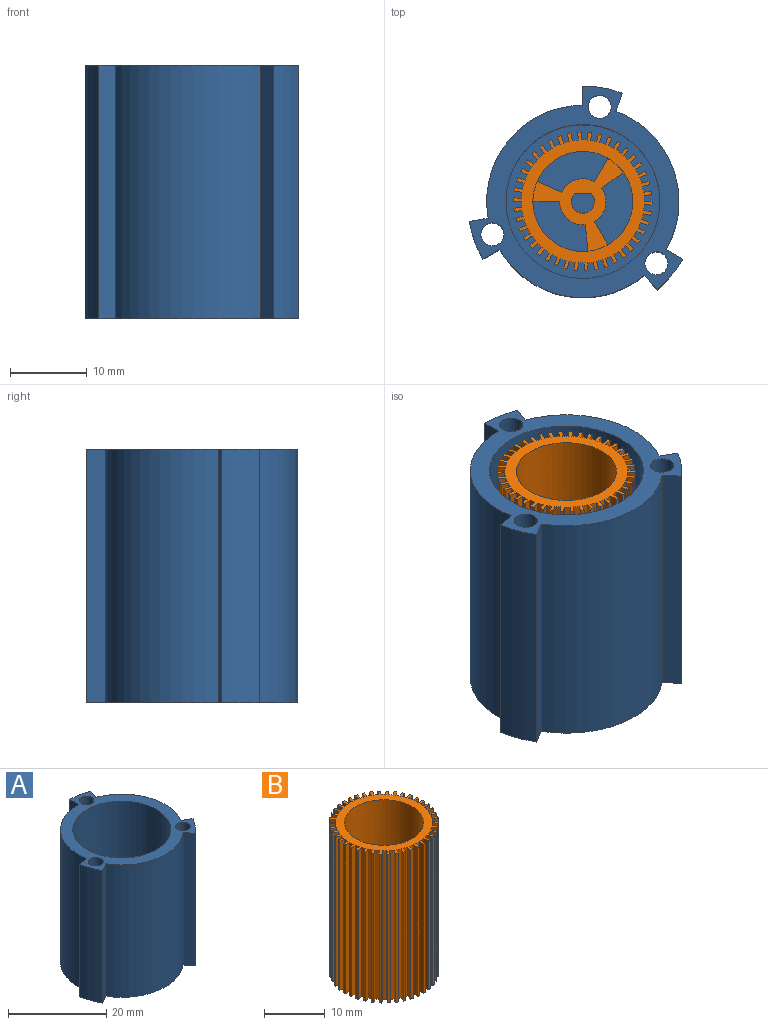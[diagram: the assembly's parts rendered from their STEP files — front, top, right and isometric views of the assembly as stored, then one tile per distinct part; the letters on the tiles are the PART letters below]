
ASSEMBLY  parts=2 mates=1
PART A: 22 faces, bbox 27.8x27.5x33 mm
  f0: plane 33x2.35mm, normal (0.94,-0.34,0), area 82.5mm2, adj f1,f14,f16,f18
  f1: cylinder r=15mm len=33mm, axis (0,0,-1), area 172.8mm2, adj f0,f2,f16,f18
  f2: plane 33x2.5mm, normal (-1,0,0), area 82.5mm2, adj f1,f3,f16,f18
  f3: cylinder r=12.5mm len=33mm, axis (0,0,-1), area 719.9mm2, adj f2,f4,f16,f18
  f4: plane 33x2.46mm, normal (-0.17,0.98,0), area 82.5mm2, adj f3,f5,f16,f18
  f5: cylinder r=15mm len=33mm, axis (0,0,-1), area 172.8mm2, adj f4,f6,f16,f18
  f6: plane 33x2.17mm, normal (0.5,-0.87,0), area 82.5mm2, adj f5,f7,f16,f18
  f7: cylinder r=12.5mm len=33mm, axis (0,0,-1), area 719.9mm2, adj f6,f8,f16,f18
  f8: plane 33x1.92mm, normal (-0.77,-0.64,0), area 82.5mm2, adj f7,f9,f16,f18
  f9: cylinder r=15mm len=33mm, axis (0,0,-1), area 172.8mm2, adj f8,f10,f16,f18
  f10: plane 33x2.17mm, normal (0.5,0.87,0), area 82.5mm2, adj f9,f14,f16,f18
  f11: cylinder r=1.5mm len=33mm, axis (0,0,-1), area 311mm2, adj f16,f18
  f12: cylinder r=1.5mm len=33mm, axis (0,0,-1), area 311mm2, adj f16,f18
  f13: cylinder r=1.5mm len=33mm, axis (0,0,-1), area 311mm2, adj f16,f18
  f14: cylinder r=12.5mm len=33mm, axis (0,0,-1), area 719.9mm2, adj f0,f10,f16,f18
  f15: plane 20x20mm, normal (0,0,1), area 307.9mm2, adj f17,f20,f21
  f16: plane 27.76x27.5mm, normal (0,0,-1), area 505.7mm2, adj f0,f1,f2,f3,f4,f5,f6,f7
  f17: cylinder r=10mm len=30mm, axis (0,0,-1), area 1885mm2, adj f15,f18
  f18: plane 27.76x27.5mm, normal (0,0,1), area 191.5mm2, adj f0,f1,f2,f3,f4,f5,f6,f7
  f19: plane 3x2.5mm, normal (0,0,1), area 6.3mm2, adj f20,f21
  f20: cylinder r=1.5mm len=17mm, axis (0,0,-1), area 117.3mm2, adj f15,f19,f21
  f21: plane 17x2.24mm, normal (0,1,0), area 38mm2, adj f15,f19,f20
PART B: 183 faces, bbox 18x18x30 mm
  f0: plane 18x18mm, normal (0,0,-1), area 129.9mm2, adj f1,f2,f3,f4,f5,f6,f7,f8
  f1: cylinder r=3mm len=10mm, axis (0,0,-1), area 50.3mm2, adj f0,f176,f179,f182
  f2: cylinder r=3mm len=10mm, axis (0,0,-1), area 50.3mm2, adj f0,f176,f177,f180
  f3: cylinder r=3mm len=10mm, axis (0,0,-1), area 50.3mm2, adj f0,f176,f178,f181
  f4: cylinder r=6.5mm len=30mm, axis (0,0,-1), area 1143.5mm2, adj f0,f173,f176,f177,f178,f179,f180,f181
  f5: cylinder r=8mm len=30mm, axis (0,0,-1), area 23.3mm2, adj f0,f6,f172,f173
  f6: plane 30x1mm, normal (-0.05,-1,0), area 30mm2, adj f0,f5,f7,f173
  f7: cylinder r=9mm len=30mm, axis (0,0,-1), area 14.1mm2, adj f0,f6,f8,f173
  f8: plane 30x1mm, normal (0,1,0), area 30mm2, adj f0,f7,f9,f173
  f9: cylinder r=8mm len=30mm, axis (0,0,-1), area 23.3mm2, adj f0,f8,f10,f173
  f10: plane 30x1mm, normal (0.1,-1,0), area 30mm2, adj f0,f9,f11,f173
  f11: cylinder r=9mm len=30mm, axis (0,0,-1), area 14.1mm2, adj f0,f10,f12,f173
  f12: plane 30x0.99mm, normal (-0.15,0.99,0), area 30mm2, adj f0,f11,f13,f173
  f13: cylinder r=8mm len=30mm, axis (0,0,-1), area 23.3mm2, adj f0,f12,f14,f173
  f14: plane 30x0.97mm, normal (0.24,-0.97,0), area 30mm2, adj f0,f13,f15,f173
  f15: cylinder r=9mm len=30mm, axis (0,0,-1), area 14.1mm2, adj f0,f14,f16,f173
  f16: plane 30x0.96mm, normal (-0.29,0.96,0), area 30mm2, adj f0,f15,f17,f173
  f17: cylinder r=8mm len=30mm, axis (0,0,-1), area 23.3mm2, adj f0,f16,f18,f173
  f18: plane 30x0.92mm, normal (0.39,-0.92,0), area 30mm2, adj f0,f17,f19,f173
  f19: cylinder r=9mm len=30mm, axis (0,0,-1), area 14.1mm2, adj f0,f18,f20,f173
  f20: plane 30x0.9mm, normal (-0.43,0.9,0), area 30mm2, adj f0,f19,f21,f173
  f21: cylinder r=8mm len=30mm, axis (0,0,-1), area 23.3mm2, adj f0,f20,f22,f173
  f22: plane 30x0.85mm, normal (0.52,-0.85,0), area 30mm2, adj f0,f21,f23,f173
  f23: cylinder r=9mm len=30mm, axis (0,0,-1), area 14.1mm2, adj f0,f22,f24,f173
  f24: plane 30x0.83mm, normal (-0.56,0.83,0), area 30mm2, adj f0,f23,f25,f173
  f25: cylinder r=8mm len=30mm, axis (0,0,-1), area 23.3mm2, adj f0,f24,f26,f173
  f26: plane 30x0.77mm, normal (0.64,-0.77,0), area 30mm2, adj f0,f25,f27,f173
  f27: cylinder r=9mm len=30mm, axis (0,0,-1), area 14.1mm2, adj f0,f26,f28,f173
  f28: plane 30x0.73mm, normal (-0.68,0.73,0), area 30mm2, adj f0,f27,f29,f173
  f29: cylinder r=8mm len=30mm, axis (0,0,-1), area 23.3mm2, adj f0,f28,f30,f173
  f30: plane 30x0.75mm, normal (0.75,-0.66,0), area 30mm2, adj f0,f29,f31,f173
  f31: cylinder r=9mm len=30mm, axis (0,0,-1), area 14.1mm2, adj f0,f30,f32,f173
  f32: plane 30x0.78mm, normal (-0.78,0.62,0), area 30mm2, adj f0,f31,f33,f173
  f33: cylinder r=8mm len=30mm, axis (0,0,-1), area 23.3mm2, adj f0,f32,f34,f173
  f34: plane 30x0.84mm, normal (0.84,-0.54,0), area 30mm2, adj f0,f33,f35,f173
  f35: cylinder r=9mm len=30mm, axis (0,0,-1), area 14.1mm2, adj f0,f34,f36,f173
  f36: plane 30x0.87mm, normal (-0.87,0.5,0), area 30mm2, adj f0,f35,f37,f173
  f37: cylinder r=8mm len=30mm, axis (0,0,-1), area 23.3mm2, adj f0,f36,f38,f173
  f38: plane 30x0.91mm, normal (0.91,-0.41,0), area 30mm2, adj f0,f37,f39,f173
  f39: cylinder r=9mm len=30mm, axis (0,0,-1), area 14.1mm2, adj f0,f38,f40,f173
  f40: plane 30x0.93mm, normal (-0.93,0.37,0), area 30mm2, adj f0,f39,f41,f173
  f41: cylinder r=8mm len=30mm, axis (0,0,-1), area 23.3mm2, adj f0,f40,f42,f173
  f42: plane 30x0.96mm, normal (0.96,-0.27,0), area 30mm2, adj f0,f41,f43,f173
  f43: cylinder r=9mm len=30mm, axis (0,0,-1), area 14.1mm2, adj f0,f42,f44,f173
  f44: plane 30x0.98mm, normal (-0.97,0.22,0), area 30mm2, adj f0,f43,f45,f173
  f45: cylinder r=8mm len=30mm, axis (0,0,-1), area 23.3mm2, adj f0,f44,f46,f173
  f46: plane 30x0.99mm, normal (0.99,-0.13,0), area 30mm2, adj f0,f45,f47,f173
  f47: cylinder r=9mm len=30mm, axis (0,0,-1), area 14.1mm2, adj f0,f46,f48,f173
  f48: plane 30x1mm, normal (-1,0.07,0), area 30mm2, adj f0,f47,f49,f173
  f49: cylinder r=8mm len=30mm, axis (0,0,-1), area 23.3mm2, adj f0,f48,f50,f173
  f50: plane 30x1mm, normal (1,0.02,0), area 30mm2, adj f0,f49,f51,f173
  f51: cylinder r=9mm len=30mm, axis (0,0,-1), area 14.1mm2, adj f0,f50,f52,f173
  f52: plane 30x1mm, normal (-1,-0.07,0), area 30mm2, adj f0,f51,f53,f173
  f53: cylinder r=8mm len=30mm, axis (0,0,-1), area 23.3mm2, adj f0,f52,f54,f173
  f54: plane 30x0.99mm, normal (0.99,0.17,0), area 30mm2, adj f0,f53,f55,f173
  f55: cylinder r=9mm len=30mm, axis (0,0,-1), area 14.1mm2, adj f0,f54,f56,f173
  f56: plane 30x0.98mm, normal (-0.97,-0.22,0), area 30mm2, adj f0,f55,f57,f173
  f57: cylinder r=8mm len=30mm, axis (0,0,-1), area 23.3mm2, adj f0,f56,f58,f173
  f58: plane 30x0.95mm, normal (0.95,0.32,0), area 30mm2, adj f0,f57,f59,f173
  f59: cylinder r=9mm len=30mm, axis (0,0,-1), area 14.1mm2, adj f0,f58,f60,f173
  f60: plane 30x0.93mm, normal (-0.93,-0.37,0), area 30mm2, adj f0,f59,f61,f173
  f61: cylinder r=8mm len=30mm, axis (0,0,-1), area 23.3mm2, adj f0,f60,f62,f173
  f62: plane 30x0.89mm, normal (0.89,0.45,0), area 30mm2, adj f0,f61,f63,f173
  f63: cylinder r=9mm len=30mm, axis (0,0,-1), area 14.1mm2, adj f0,f62,f64,f173
  f64: plane 30x0.87mm, normal (-0.87,-0.5,0), area 30mm2, adj f0,f63,f65,f173
  f65: cylinder r=8mm len=30mm, axis (0,0,-1), area 23.3mm2, adj f0,f64,f66,f173
  f66: plane 30x0.81mm, normal (0.81,0.58,0), area 30mm2, adj f0,f65,f67,f173
  f67: cylinder r=9mm len=30mm, axis (0,0,-1), area 14.1mm2, adj f0,f66,f68,f173
  f68: plane 30x0.78mm, normal (-0.78,-0.62,0), area 30mm2, adj f0,f67,f69,f173
  f69: cylinder r=8mm len=30mm, axis (0,0,-1), area 23.3mm2, adj f0,f68,f70,f173
  f70: plane 30x0.72mm, normal (0.72,0.7,0), area 30mm2, adj f0,f69,f71,f173
  f71: cylinder r=9mm len=30mm, axis (0,0,-1), area 14.1mm2, adj f0,f70,f72,f173
  f72: plane 30x0.73mm, normal (-0.68,-0.73,0), area 30mm2, adj f0,f71,f73,f173
  f73: cylinder r=8mm len=30mm, axis (0,0,-1), area 23.3mm2, adj f0,f72,f74,f173
  f74: plane 30x0.8mm, normal (0.61,0.8,0), area 30mm2, adj f0,f73,f75,f173
  f75: cylinder r=9mm len=30mm, axis (0,0,-1), area 14.1mm2, adj f0,f74,f76,f173
  f76: plane 30x0.83mm, normal (-0.56,-0.83,0), area 30mm2, adj f0,f75,f77,f173
  f77: cylinder r=8mm len=30mm, axis (0,0,-1), area 23.3mm2, adj f0,f76,f78,f173
  f78: plane 30x0.88mm, normal (0.48,0.88,0), area 30mm2, adj f0,f77,f79,f173
  f79: cylinder r=9mm len=30mm, axis (0,0,-1), area 14.1mm2, adj f0,f78,f80,f173
  f80: plane 30x0.9mm, normal (-0.43,-0.9,0), area 30mm2, adj f0,f79,f81,f173
  f81: cylinder r=8mm len=30mm, axis (0,0,-1), area 23.3mm2, adj f0,f80,f82,f173
  f82: plane 30x0.94mm, normal (0.34,0.94,0), area 30mm2, adj f0,f81,f83,f173
  f83: cylinder r=9mm len=30mm, axis (0,0,-1), area 14.1mm2, adj f0,f82,f84,f173
  f84: plane 30x0.96mm, normal (-0.29,-0.96,0), area 30mm2, adj f0,f83,f85,f173
  f85: cylinder r=8mm len=30mm, axis (0,0,-1), area 23.3mm2, adj f0,f84,f86,f173
  f86: plane 30x0.98mm, normal (0.2,0.98,0), area 30mm2, adj f0,f85,f87,f173
  f87: cylinder r=9mm len=30mm, axis (0,0,-1), area 14.1mm2, adj f0,f86,f88,f173
  f88: plane 30x0.99mm, normal (-0.15,-0.99,0), area 30mm2, adj f0,f87,f89,f173
  f89: cylinder r=8mm len=30mm, axis (0,0,-1), area 23.3mm2, adj f0,f88,f90,f173
  f90: plane 30x1mm, normal (0.05,1,0), area 30mm2, adj f0,f89,f91,f173
  f91: cylinder r=9mm len=30mm, axis (0,0,-1), area 14.1mm2, adj f0,f90,f92,f173
  f92: plane 30x1mm, normal (0,-1,0), area 30mm2, adj f0,f91,f93,f173
  f93: cylinder r=8mm len=30mm, axis (0,0,-1), area 23.3mm2, adj f0,f92,f94,f173
  f94: plane 30x1mm, normal (-0.1,1,0), area 30mm2, adj f0,f93,f95,f173
  f95: cylinder r=9mm len=30mm, axis (0,0,-1), area 14.1mm2, adj f0,f94,f96,f173
  f96: plane 30x0.99mm, normal (0.15,-0.99,0), area 30mm2, adj f0,f95,f97,f173
  f97: cylinder r=8mm len=30mm, axis (0,0,-1), area 23.3mm2, adj f0,f96,f98,f173
  f98: plane 30x0.97mm, normal (-0.24,0.97,0), area 30mm2, adj f0,f97,f99,f173
  f99: cylinder r=9mm len=30mm, axis (0,0,-1), area 14.1mm2, adj f0,f98,f100,f173
  f100: plane 30x0.96mm, normal (0.29,-0.96,0), area 30mm2, adj f0,f99,f101,f173
  f101: cylinder r=8mm len=30mm, axis (0,0,-1), area 23.3mm2, adj f0,f100,f102,f173
  f102: plane 30x0.92mm, normal (-0.39,0.92,0), area 30mm2, adj f0,f101,f103,f173
  f103: cylinder r=9mm len=30mm, axis (0,0,-1), area 14.1mm2, adj f0,f102,f104,f173
  f104: plane 30x0.9mm, normal (0.43,-0.9,0), area 30mm2, adj f0,f103,f105,f173
  f105: cylinder r=8mm len=30mm, axis (0,0,-1), area 23.3mm2, adj f0,f104,f106,f173
  f106: plane 30x0.85mm, normal (-0.52,0.85,0), area 30mm2, adj f0,f105,f107,f173
  f107: cylinder r=9mm len=30mm, axis (0,0,-1), area 14.1mm2, adj f0,f106,f108,f173
  f108: plane 30x0.83mm, normal (0.56,-0.83,0), area 30mm2, adj f0,f107,f109,f173
  f109: cylinder r=8mm len=30mm, axis (0,0,-1), area 23.3mm2, adj f0,f108,f110,f173
  f110: plane 30x0.77mm, normal (-0.64,0.77,0), area 30mm2, adj f0,f109,f111,f173
  f111: cylinder r=9mm len=30mm, axis (0,0,-1), area 14.1mm2, adj f0,f110,f112,f173
  f112: plane 30x0.73mm, normal (0.68,-0.73,0), area 30mm2, adj f0,f111,f113,f173
  f113: cylinder r=8mm len=30mm, axis (0,0,-1), area 23.3mm2, adj f0,f112,f114,f173
  f114: plane 30x0.75mm, normal (-0.75,0.66,0), area 30mm2, adj f0,f113,f115,f173
  f115: cylinder r=9mm len=30mm, axis (0,0,-1), area 14.1mm2, adj f0,f114,f116,f173
  f116: plane 30x0.78mm, normal (0.78,-0.62,0), area 30mm2, adj f0,f115,f117,f173
  f117: cylinder r=8mm len=30mm, axis (0,0,-1), area 23.3mm2, adj f0,f116,f118,f173
  f118: plane 30x0.84mm, normal (-0.84,0.54,0), area 30mm2, adj f0,f117,f119,f173
  f119: cylinder r=9mm len=30mm, axis (0,0,-1), area 14.1mm2, adj f0,f118,f120,f173
  f120: plane 30x0.87mm, normal (0.87,-0.5,0), area 30mm2, adj f0,f119,f121,f173
  f121: cylinder r=8mm len=30mm, axis (0,0,-1), area 23.3mm2, adj f0,f120,f122,f173
  f122: plane 30x0.91mm, normal (-0.91,0.41,0), area 30mm2, adj f0,f121,f123,f173
  f123: cylinder r=9mm len=30mm, axis (0,0,-1), area 14.1mm2, adj f0,f122,f124,f173
  f124: plane 30x0.93mm, normal (0.93,-0.37,0), area 30mm2, adj f0,f123,f125,f173
  f125: cylinder r=8mm len=30mm, axis (0,0,-1), area 23.3mm2, adj f0,f124,f126,f173
  f126: plane 30x0.96mm, normal (-0.96,0.27,0), area 30mm2, adj f0,f125,f127,f173
  f127: cylinder r=9mm len=30mm, axis (0,0,-1), area 14.1mm2, adj f0,f126,f128,f173
  f128: plane 30x0.98mm, normal (0.97,-0.22,0), area 30mm2, adj f0,f127,f129,f173
  f129: cylinder r=8mm len=30mm, axis (0,0,-1), area 23.3mm2, adj f0,f128,f130,f173
  f130: plane 30x0.99mm, normal (-0.99,0.13,0), area 30mm2, adj f0,f129,f131,f173
  f131: cylinder r=9mm len=30mm, axis (0,0,-1), area 14.1mm2, adj f0,f130,f132,f173
  f132: plane 30x1mm, normal (1,-0.07,0), area 30mm2, adj f0,f131,f133,f173
  f133: cylinder r=8mm len=30mm, axis (0,0,-1), area 23.3mm2, adj f0,f132,f134,f173
  f134: plane 30x1mm, normal (-1,-0.02,0), area 30mm2, adj f0,f133,f135,f173
  f135: cylinder r=9mm len=30mm, axis (0,0,-1), area 14.1mm2, adj f0,f134,f136,f173
  f136: plane 30x1mm, normal (1,0.07,0), area 30mm2, adj f0,f135,f137,f173
  f137: cylinder r=8mm len=30mm, axis (0,0,-1), area 23.3mm2, adj f0,f136,f138,f173
  f138: plane 30x0.99mm, normal (-0.99,-0.17,0), area 30mm2, adj f0,f137,f139,f173
  f139: cylinder r=9mm len=30mm, axis (0,0,-1), area 14.1mm2, adj f0,f138,f140,f173
  f140: plane 30x0.98mm, normal (0.97,0.22,0), area 30mm2, adj f0,f139,f141,f173
  f141: cylinder r=8mm len=30mm, axis (0,0,-1), area 23.3mm2, adj f0,f140,f142,f173
  f142: plane 30x0.95mm, normal (-0.95,-0.32,0), area 30mm2, adj f0,f141,f143,f173
  f143: cylinder r=9mm len=30mm, axis (0,0,-1), area 14.1mm2, adj f0,f142,f144,f173
  f144: plane 30x0.93mm, normal (0.93,0.37,0), area 30mm2, adj f0,f143,f145,f173
  f145: cylinder r=8mm len=30mm, axis (0,0,-1), area 23.3mm2, adj f0,f144,f146,f173
  f146: plane 30x0.89mm, normal (-0.89,-0.45,0), area 30mm2, adj f0,f145,f147,f173
  f147: cylinder r=9mm len=30mm, axis (0,0,-1), area 14.1mm2, adj f0,f146,f148,f173
  f148: plane 30x0.87mm, normal (0.87,0.5,0), area 30mm2, adj f0,f147,f149,f173
  f149: cylinder r=8mm len=30mm, axis (0,0,-1), area 23.3mm2, adj f0,f148,f150,f173
  f150: plane 30x0.81mm, normal (-0.81,-0.58,0), area 30mm2, adj f0,f149,f151,f173
  f151: cylinder r=9mm len=30mm, axis (0,0,-1), area 14.1mm2, adj f0,f150,f152,f173
  f152: plane 30x0.78mm, normal (0.78,0.62,0), area 30mm2, adj f0,f151,f153,f173
  f153: cylinder r=8mm len=30mm, axis (0,0,-1), area 23.3mm2, adj f0,f152,f154,f173
  f154: plane 30x0.72mm, normal (-0.72,-0.7,0), area 30mm2, adj f0,f153,f155,f173
  f155: cylinder r=9mm len=30mm, axis (0,0,-1), area 14.1mm2, adj f0,f154,f156,f173
  f156: plane 30x0.73mm, normal (0.68,0.73,0), area 30mm2, adj f0,f155,f157,f173
  f157: cylinder r=8mm len=30mm, axis (0,0,-1), area 23.3mm2, adj f0,f156,f158,f173
  f158: plane 30x0.8mm, normal (-0.61,-0.8,0), area 30mm2, adj f0,f157,f159,f173
  f159: cylinder r=9mm len=30mm, axis (0,0,-1), area 14.1mm2, adj f0,f158,f160,f173
  f160: plane 30x0.83mm, normal (0.56,0.83,0), area 30mm2, adj f0,f159,f161,f173
  f161: cylinder r=8mm len=30mm, axis (0,0,-1), area 23.3mm2, adj f0,f160,f162,f173
  f162: plane 30x0.88mm, normal (-0.48,-0.88,0), area 30mm2, adj f0,f161,f163,f173
  f163: cylinder r=9mm len=30mm, axis (0,0,-1), area 14.1mm2, adj f0,f162,f164,f173
  f164: plane 30x0.9mm, normal (0.43,0.9,0), area 30mm2, adj f0,f163,f165,f173
  f165: cylinder r=8mm len=30mm, axis (0,0,-1), area 23.3mm2, adj f0,f164,f166,f173
  f166: plane 30x0.94mm, normal (-0.34,-0.94,0), area 30mm2, adj f0,f165,f167,f173
  f167: cylinder r=9mm len=30mm, axis (0,0,-1), area 14.1mm2, adj f0,f166,f168,f173
  f168: plane 30x0.96mm, normal (0.29,0.96,0), area 30mm2, adj f0,f167,f169,f173
  f169: cylinder r=8mm len=30mm, axis (0,0,-1), area 23.3mm2, adj f0,f168,f170,f173
  f170: plane 30x0.98mm, normal (-0.2,-0.98,0), area 30mm2, adj f0,f169,f171,f173
  f171: cylinder r=9mm len=30mm, axis (0,0,-1), area 14.1mm2, adj f0,f170,f172,f173
  f172: plane 30x0.99mm, normal (0.15,0.99,0), area 30mm2, adj f0,f5,f171,f173
  f173: plane 18x18mm, normal (0,0,1), area 87mm2, adj f4,f5,f6,f7,f8,f9,f10,f11
  f174: cylinder r=1.5mm len=10mm, axis (0,0,-1), area 69mm2, adj f0,f175,f176
  f175: plane 10x2.24mm, normal (0,-1,0), area 22.4mm2, adj f0,f174,f176
  f176: plane 12.09x11.76mm, normal (0,0,1), area 42.9mm2, adj f1,f2,f3,f4,f174,f175,f177,f178
  f177: plane 10x3.03mm, normal (-0.87,0.5,0), area 35mm2, adj f0,f2,f4,f176
  f178: plane 10x2.83mm, normal (0.59,-0.81,0), area 35mm2, adj f0,f3,f4,f176
  f179: plane 10x3.5mm, normal (0,-1,0), area 35mm2, adj f0,f1,f4,f176
  f180: plane 10x3.2mm, normal (0.41,0.91,0), area 35mm2, adj f0,f2,f4,f176
  f181: plane 10x3.03mm, normal (0.87,0.5,0), area 35mm2, adj f0,f3,f4,f176
  f182: plane 10x3.48mm, normal (-0.99,-0.1,0), area 35mm2, adj f0,f1,f4,f176
PLACE A t=(-24.51,14.28,-28.31)mm fixed
PLACE B t=(-24.51,14.28,-25.51)mm
MATE slider A.f1 <-> B.f1  axis (0,0,-1) through (-24.51,14.28,-8.31)mm
